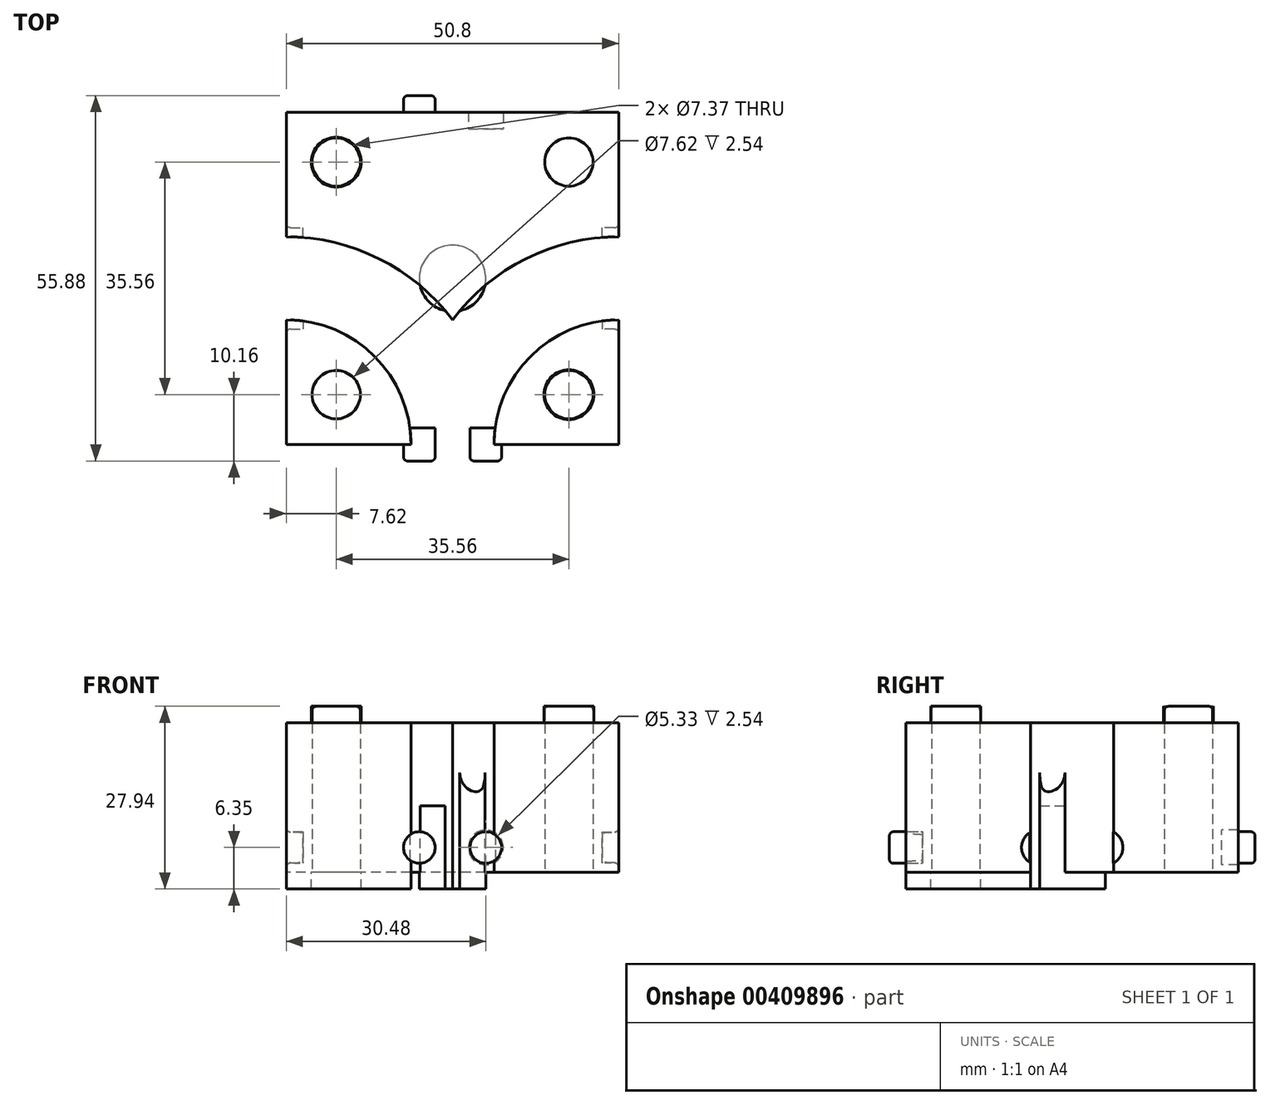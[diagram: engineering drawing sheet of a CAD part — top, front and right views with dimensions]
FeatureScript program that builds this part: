
annotation { "Feature Type Name" : "Feature", "Feature Type Description" : "" }
export const myFeature = defineFeature(function(context is Context, id is Id, definition is map)
    precondition{}
    {
        {
            var Q0;
            Q0=qCreatedBy(makeId("Top.planeOp"),FACE);
            var sketch = newSketch(context, id + "F0", { "sketchPlane" : qUnion([Q0])});
            skLineSegment(sketch, "E0.bottom", {"start": v(25.4, 25.4) * mm, "end": v(-25.4, 25.4) * mm});
            skLineSegment(sketch, "E0.top", {"start": v(25.4, -25.4) * mm, "end": v(-25.4, -25.4) * mm});
            skLineSegment(sketch, "E0.left", {"start": v(25.4, 25.4) * mm, "end": v(25.4, -25.4) * mm});
            skLineSegment(sketch, "E0.right", {"start": v(-25.4, 25.4) * mm, "end": v(-25.4, -25.4) * mm});
            skPoint(sketch, "E0.middle", {"position": v(0, 0) * mm});
            skPoint(sketch, "E1", {"position": v(17.78, 17.78) * mm});
            skPoint(sketch, "E2", {"position": v(17.78, 25.4) * mm});
            skLineSegment(sketch, "E3", {"start": v(17.78, 17.78) * mm, "end": v(17.78, 25.4) * mm, "construction": true});
            skCircle(sketch, "E4", {"center": v(17.78, 17.78) * mm, "radius": 3.81 * mm, "construction": true});
            skCircle(sketch, "E5.MirrorC", {"center": v(-17.78, 17.78) * mm, "radius": 3.81 * mm});
            skCircle(sketch, "E6.MirrorC", {"center": v(17.78, -17.78) * mm, "radius": 3.81 * mm});
            skCircle(sketch, "E7.MirrorC", {"center": v(-17.78, -17.78) * mm, "radius": 3.81 * mm});
            skPoint(sketch, "E8", {"position": v(25.4, 0) * mm});
            skPoint(sketch, "E9", {"position": v(-25.4, 0) * mm});
            skCircle(sketch, "E10", {"center": v(17.78, 17.78) * mm, "radius": 3.68 * mm});
            skCircle(sketch, "E11.MirrorC", {"center": v(-17.78, 17.78) * mm, "radius": 3.68 * mm});
            skCircle(sketch, "E12.MirrorC", {"center": v(-17.78, -17.78) * mm, "radius": 3.68 * mm});
            skCircle(sketch, "E13.MirrorC", {"center": v(17.78, -17.78) * mm, "radius": 3.68 * mm});
            skLineSegment(sketch, "E14", {"start": v(-25.4, 0) * mm, "end": v(25.4, 0) * mm, "construction": true});
            skLineSegment(sketch, "E15", {"start": v(0, 25.4) * mm, "end": v(0, -25.4) * mm, "construction": true});
            skCircle(sketch, "E16", {"center": v(0, 0) * mm, "radius": 2.54 * mm, "construction": true});
            skPoint(sketch, "E17", {"position": v(0, 2.54) * mm});
            skPoint(sketch, "E18", {"position": v(0, 5.08) * mm});
            skCircle(sketch, "E19", {"center": v(0, 0) * mm, "radius": 2.41 * mm});
            skCircle(sketch, "E20", {"center": v(0, 0) * mm, "radius": 2.67 * mm});
            skPoint(sketch, "E21", {"position": v(2.41, 0) * mm});
            skPoint(sketch, "E22", {"position": v(2.67, 0) * mm});
            skLineSegment(sketch, "E23", {"start": v(2.41, 0) * mm, "end": v(2.67, 0) * mm, "construction": true});
            skCircle(sketch, "E24", {"center": v(17.78, 17.78) * mm, "radius": 3.94 * mm});
            skLineSegment(sketch, "E25", {"start": v(17.78, 21.46) * mm, "end": v(17.78, 21.72) * mm, "construction": true});
            skPoint(sketch, "E25.endSnap0", {"position": v(17.78, 21.59) * mm});
            skLineSegment(sketch, "E26", {"start": v(25.4, 6.35) * mm, "end": v(25.4, -6.35) * mm});
            skPoint(sketch, "E27", {"position": v(6.35, -25.4) * mm});
            skPoint(sketch, "E28", {"position": v(-6.35, -25.4) * mm});
            skArc(sketch, "E29", {"start": v(6.35, -25.4) * mm, "mid": v(11.93, -11.93) * mm, "end": v(25.4, -6.35) * mm});
            skArc(sketch, "E30", {"start": v(-6.35, -25.4) * mm, "mid": v(-11.93, -11.93) * mm, "end": v(-25.4, -6.35) * mm});
            skPoint(sketch, "E31", {"position": v(-25.4, 6.35) * mm});
            skArc(sketch, "E32", {"start": v(25.4, 6.35) * mm, "mid": v(11.2, 3) * mm, "end": v(0, -6.35) * mm});
            skArc(sketch, "E33", {"start": v(0, -6.35) * mm, "mid": v(-11.2, 3) * mm, "end": v(-25.4, 6.35) * mm});
            skCircle(sketch, "E34", {"center": v(0, 0) * mm, "radius": 5.08 * mm});
            skPoint(sketch, "E35", {"position": v(2.54, 0) * mm});
            skLineSegment(sketch, "E36", {"start": v(17.78, 17.78) * mm, "end": v(25.4, 17.78) * mm});
            skSolve(sketch);
        }
        {
            var Q0;
            Q0=makeQuery(id+"F0.imprint","IMPRINT",FACE,{"disambiguationData":[TD([[makeQuery(id+"F0.imprint","IMPRINT",EDGE,{"derivedFrom":sQuery(id+"F0.wireOp",EDGE,"E5.MirrorC")}),1.0]])]});
            var Q1;
            {var subQ0=sQuery(id+"F0.wireOp",EDGE,"e8c6bd5a-b162-413f-9673-ee5317453a08.1.0");var subQ1=sQuery(id+"F0.wireOp",EDGE,"E0.right");var subQ2=makeQuery(id+"F0.imprint","INTERSECT",VERTEX,{"derivedFrom":[subQ1,subQ0]});Q1=makeQuery(id+"F0.imprint","IMPRINT",FACE,{"disambiguationData":[TD([[makeQuery(id+"F0.imprint","IMPRINT",EDGE,{"disambiguationData":[TD([[subQ2,-1.0]])],"derivedFrom":subQ1}),1.0]])]});}
            var Q2;
            Q2=makeQuery(id+"F0.imprint","IMPRINT",FACE,{"disambiguationData":[TD([[makeQuery(id+"F0.imprint","IMPRINT",EDGE,{"derivedFrom":sQuery(id+"F0.wireOp",EDGE,"E7.MirrorC")}),-1.0]])]});
            var Q3;
            Q3=makeQuery(id+"F0.imprint","IMPRINT",FACE,{"disambiguationData":[TD([[makeQuery(id+"F0.imprint","IMPRINT",EDGE,{"derivedFrom":sQuery(id+"F0.wireOp",EDGE,"E5.MirrorC")}),-1.0]])]});
            var Q4;
            Q4=makeQuery(id+"F0.imprint","IMPRINT",FACE,{"disambiguationData":[TD([[makeQuery(id+"F0.imprint","IMPRINT",EDGE,{"derivedFrom":sQuery(id+"F0.wireOp",EDGE,"E7.MirrorC")}),1.0]])]});
            var Q5;
            Q5=makeQuery(id+"F0.imprint","IMPRINT",FACE,{"disambiguationData":[TD([[makeQuery(id+"F0.imprint","IMPRINT",EDGE,{"derivedFrom":sQuery(id+"F0.wireOp",EDGE,"E6.MirrorC")}),-1.0]])]});
            var Q6;
            Q6=makeQuery(id+"F0.imprint","IMPRINT",FACE,{"disambiguationData":[TD([[makeQuery(id+"F0.imprint","IMPRINT",EDGE,{"derivedFrom":sQuery(id+"F0.wireOp",EDGE,"E10")}),-1.0]])]});
            var Q7;
            Q7=makeQuery(id+"F0.imprint","IMPRINT",FACE,{"disambiguationData":[TD([[makeQuery(id+"F0.imprint","IMPRINT",EDGE,{"derivedFrom":sQuery(id+"F0.wireOp",EDGE,"E19")}),1.0]])]});
            var Q8;
            Q8=makeQuery(id+"F0.imprint","IMPRINT",FACE,{"disambiguationData":[TD([[makeQuery(id+"F0.imprint","IMPRINT",EDGE,{"derivedFrom":sQuery(id+"F0.wireOp",EDGE,"E12.MirrorC")}),1.0]])]});
            var Q9;
            Q9=makeQuery(id+"F0.imprint","IMPRINT",FACE,{"disambiguationData":[TD([[makeQuery(id+"F0.imprint","IMPRINT",EDGE,{"derivedFrom":sQuery(id+"F0.wireOp",EDGE,"E7.MirrorC")}),-1.0]])]});
            var Q10;
            Q10=makeQuery(id+"F0.imprint","IMPRINT",FACE,{"disambiguationData":[TD([[makeQuery(id+"F0.imprint","IMPRINT",EDGE,{"derivedFrom":sQuery(id+"F0.wireOp",EDGE,"E13.MirrorC")}),-1.0]])]});
            var Q11;
            Q11=makeQuery(id+"F0.imprint","IMPRINT",FACE,{"disambiguationData":[TD([[makeQuery(id+"F0.imprint","IMPRINT",EDGE,{"derivedFrom":sQuery(id+"F0.wireOp",EDGE,"E6.MirrorC")}),1.0]])]});
            var Q12;
            Q12=makeQuery(id+"F0.imprint","IMPRINT",FACE,{"disambiguationData":[TD([[makeQuery(id+"F0.imprint","IMPRINT",EDGE,{"derivedFrom":sQuery(id+"F0.wireOp",EDGE,"E11.MirrorC")}),-1.0]])]});
            var Q13;
            Q13=makeQuery(id+"F0.imprint","IMPRINT",FACE,{"disambiguationData":[TD([[makeQuery(id+"F0.imprint","IMPRINT",EDGE,{"derivedFrom":sQuery(id+"F0.wireOp",EDGE,"E10")}),1.0]])]});
            var Q14;
            Q14=makeQuery(id+"F0.imprint","IMPRINT",FACE,{"disambiguationData":[TD([[makeQuery(id+"F0.imprint","IMPRINT",EDGE,{"derivedFrom":sQuery(id+"F0.wireOp",EDGE,"E19")}),-1.0]])]});
            var Q15;
            Q15=makeQuery(id+"F0.imprint","IMPRINT",FACE,{"disambiguationData":[TD([[makeQuery(id+"F0.imprint","IMPRINT",EDGE,{"derivedFrom":sQuery(id+"F0.wireOp",EDGE,"E20")}),-1.0]])]});
            var Q16;
            {var subQ0=sQuery(id+"F0.wireOp",EDGE,"E33");var subQ1=sQuery(id+"F0.wireOp",EDGE,"E32");var subQ2=makeQuery(id+"F0.imprint","INTERSECT",VERTEX,{"derivedFrom":[subQ1,subQ0]});Q16=makeQuery(id+"F0.imprint","IMPRINT",FACE,{"disambiguationData":[TD([[makeQuery(id+"F0.imprint","IMPRINT",EDGE,{"disambiguationData":[TD([[subQ2,1.0]])],"derivedFrom":subQ1}),-1.0]])]});}
            extrude(context, id + "F1", {"entities" : qUnion([Q0, Q1, Q2, Q3, Q4, Q5, Q6, Q7, Q8, Q9, Q10, Q11, Q12, Q13, Q14, Q15, Q16]), "depth" : 12.7 * mm});
        }
        {
            var Q0;
            Q0=makeQuery(id+"F0.imprint","IMPRINT",FACE,{"disambiguationData":[TD([[makeQuery(id+"F0.imprint","IMPRINT",EDGE,{"derivedFrom":sQuery(id+"F0.wireOp",EDGE,"E12.MirrorC")}),1.0]])]});
            var Q1;
            Q1=makeQuery(id+"F0.imprint","IMPRINT",FACE,{"disambiguationData":[TD([[makeQuery(id+"F0.imprint","IMPRINT",EDGE,{"derivedFrom":sQuery(id+"F0.wireOp",EDGE,"E11.MirrorC")}),-1.0]])]});
            var Q2;
            Q2=makeQuery(id+"F0.imprint","IMPRINT",FACE,{"disambiguationData":[TD([[makeQuery(id+"F0.imprint","IMPRINT",EDGE,{"derivedFrom":sQuery(id+"F0.wireOp",EDGE,"E10")}),1.0]])]});
            var Q3;
            Q3=makeQuery(id+"F0.imprint","IMPRINT",FACE,{"disambiguationData":[TD([[makeQuery(id+"F0.imprint","IMPRINT",EDGE,{"derivedFrom":sQuery(id+"F0.wireOp",EDGE,"E13.MirrorC")}),-1.0]])]});
            extrude(context, id + "F2", {"entities" : qUnion([Q0, Q1, Q2, Q3]), "operationType" : NewBodyOperationType.ADD, "depth" : 15.24 * mm});
        }
        {
            var Q0;
            Q0=makeQuery(id+"F0.imprint","IMPRINT",FACE,{"disambiguationData":[TD([[makeQuery(id+"F0.imprint","IMPRINT",EDGE,{"derivedFrom":sQuery(id+"F0.wireOp",EDGE,"E7.MirrorC")}),-1.0]])]});
            var Q1;
            Q1=makeQuery(id+"F0.imprint","IMPRINT",FACE,{"disambiguationData":[TD([[makeQuery(id+"F0.imprint","IMPRINT",EDGE,{"derivedFrom":sQuery(id+"F0.wireOp",EDGE,"E19")}),-1.0]])]});
            var Q2;
            Q2=makeQuery(id+"F0.imprint","IMPRINT",FACE,{"disambiguationData":[TD([[makeQuery(id+"F0.imprint","IMPRINT",EDGE,{"derivedFrom":sQuery(id+"F0.wireOp",EDGE,"E19")}),1.0]])]});
            var Q3;
            {var subQ1=sQuery(id+"F0.wireOp",EDGE,"E0.bottom");Q3=makeQuery(id+"F0.imprint","IMPRINT",FACE,{"disambiguationData":[TD([[makeQuery(id+"F0.imprint","IMPRINT",EDGE,{"derivedFrom":subQ1}),1.0]])]});}
            var Q4;
            {var subQ4=sQuery(id+"F0.wireOp",EDGE,"E26");Q4=makeQuery(id+"F0.imprint","IMPRINT",FACE,{"disambiguationData":[TD([[makeQuery(id+"F0.imprint","IMPRINT",EDGE,{"derivedFrom":subQ4}),-1.0]])]});}
            var Q5;
            Q5=makeQuery(id+"F0.imprint","IMPRINT",FACE,{"disambiguationData":[TD([[makeQuery(id+"F0.imprint","IMPRINT",EDGE,{"derivedFrom":sQuery(id+"F0.wireOp",EDGE,"E13.MirrorC")}),-1.0]])]});
            var Q6;
            Q6=makeQuery(id+"F0.imprint","IMPRINT",FACE,{"disambiguationData":[TD([[makeQuery(id+"F0.imprint","IMPRINT",EDGE,{"derivedFrom":sQuery(id+"F0.wireOp",EDGE,"E6.MirrorC")}),-1.0]])]});
            var Q7;
            Q7=makeQuery(id+"F0.imprint","IMPRINT",FACE,{"disambiguationData":[TD([[makeQuery(id+"F0.imprint","IMPRINT",EDGE,{"derivedFrom":sQuery(id+"F0.wireOp",EDGE,"E6.MirrorC")}),1.0]])]});
            var Q8;
            Q8=makeQuery(id+"F0.imprint","IMPRINT",FACE,{"disambiguationData":[TD([[makeQuery(id+"F0.imprint","IMPRINT",EDGE,{"derivedFrom":sQuery(id+"F0.wireOp",EDGE,"E12.MirrorC")}),1.0]])]});
            var Q9;
            Q9=makeQuery(id+"F0.imprint","IMPRINT",FACE,{"disambiguationData":[TD([[makeQuery(id+"F0.imprint","IMPRINT",EDGE,{"derivedFrom":sQuery(id+"F0.wireOp",EDGE,"E7.MirrorC")}),1.0]])]});
            var Q10;
            Q10=makeQuery(id+"F0.imprint","IMPRINT",FACE,{"disambiguationData":[TD([[makeQuery(id+"F0.imprint","IMPRINT",EDGE,{"derivedFrom":sQuery(id+"F0.wireOp",EDGE,"E5.MirrorC")}),-1.0]])]});
            var Q11;
            Q11=makeQuery(id+"F0.imprint","IMPRINT",FACE,{"disambiguationData":[TD([[makeQuery(id+"F0.imprint","IMPRINT",EDGE,{"derivedFrom":sQuery(id+"F0.wireOp",EDGE,"E11.MirrorC")}),-1.0]])]});
            var Q12;
            Q12=makeQuery(id+"F0.imprint","IMPRINT",FACE,{"disambiguationData":[TD([[makeQuery(id+"F0.imprint","IMPRINT",EDGE,{"derivedFrom":sQuery(id+"F0.wireOp",EDGE,"E10")}),-1.0]])]});
            var Q13;
            Q13=makeQuery(id+"F0.imprint","IMPRINT",FACE,{"disambiguationData":[TD([[makeQuery(id+"F0.imprint","IMPRINT",EDGE,{"derivedFrom":sQuery(id+"F0.wireOp",EDGE,"E10")}),1.0]])]});
            var Q14;
            Q14=makeQuery(id+"F0.imprint","IMPRINT",FACE,{"disambiguationData":[TD([[makeQuery(id+"F0.imprint","IMPRINT",EDGE,{"derivedFrom":sQuery(id+"F0.wireOp",EDGE,"E20")}),-1.0]])]});
            var Q15;
            {var subQ0=sQuery(id+"F0.wireOp",EDGE,"E34");var subQ1=sQuery(id+"F0.wireOp",EDGE,"E33");var subQ2=makeQuery(id+"F0.imprint","INTERSECT",VERTEX,{"disambiguationData":[OD(0.0)],"derivedFrom":[subQ1,subQ0]});Q15=makeQuery(id+"F0.imprint","IMPRINT",FACE,{"disambiguationData":[TD([[makeQuery(id+"F0.imprint","IMPRINT",EDGE,{"disambiguationData":[TD([[subQ2,-1.0]])],"derivedFrom":subQ1}),1.0]])]});}
            var Q16;
            {var subQ0=sQuery(id+"F0.wireOp",EDGE,"E34");var subQ1=sQuery(id+"F0.wireOp",EDGE,"E32");var subQ2=makeQuery(id+"F0.imprint","INTERSECT",VERTEX,{"disambiguationData":[OD(0.0)],"derivedFrom":[subQ1,subQ0]});Q16=makeQuery(id+"F0.imprint","IMPRINT",FACE,{"disambiguationData":[TD([[makeQuery(id+"F0.imprint","IMPRINT",EDGE,{"disambiguationData":[TD([[subQ2,-1.0]])],"derivedFrom":subQ1}),1.0]])]});}
            var Q17;
            {var subQ0=sQuery(id+"F0.wireOp",EDGE,"E33");var subQ1=sQuery(id+"F0.wireOp",EDGE,"E32");var subQ2=makeQuery(id+"F0.imprint","INTERSECT",VERTEX,{"derivedFrom":[subQ1,subQ0]});Q17=makeQuery(id+"F0.imprint","IMPRINT",FACE,{"disambiguationData":[TD([[makeQuery(id+"F0.imprint","IMPRINT",EDGE,{"disambiguationData":[TD([[subQ2,1.0]])],"derivedFrom":subQ1}),-1.0]])]});}
            extrude(context, id + "F3", {"entities" : qUnion([Q0, Q1, Q2, Q3, Q4, Q5, Q6, Q7, Q8, Q9, Q10, Q11, Q12, Q13, Q14, Q15, Q16, Q17]), "operationType" : NewBodyOperationType.ADD, "oppositeDirection" : true, "depth" : 12.7 * mm});
        }
        {
            var Q0;
            Q0=makeQuery(id+"F0.imprint","IMPRINT",FACE,{"disambiguationData":[TD([[makeQuery(id+"F0.imprint","IMPRINT",EDGE,{"derivedFrom":sQuery(id+"F0.wireOp",EDGE,"E13.MirrorC")}),-1.0]])]});
            var Q1;
            Q1=makeQuery(id+"F0.imprint","IMPRINT",FACE,{"disambiguationData":[TD([[makeQuery(id+"F0.imprint","IMPRINT",EDGE,{"derivedFrom":sQuery(id+"F0.wireOp",EDGE,"E7.MirrorC")}),1.0]])]});
            var Q2;
            Q2=makeQuery(id+"F0.imprint","IMPRINT",FACE,{"disambiguationData":[TD([[makeQuery(id+"F0.imprint","IMPRINT",EDGE,{"derivedFrom":sQuery(id+"F0.wireOp",EDGE,"E12.MirrorC")}),1.0]])]});
            var Q3;
            Q3=makeQuery(id+"F0.imprint","IMPRINT",FACE,{"disambiguationData":[TD([[makeQuery(id+"F0.imprint","IMPRINT",EDGE,{"derivedFrom":sQuery(id+"F0.wireOp",EDGE,"E6.MirrorC")}),-1.0]])]});
            var Q4;
            Q4=makeQuery(id+"F0.imprint","IMPRINT",FACE,{"disambiguationData":[TD([[makeQuery(id+"F0.imprint","IMPRINT",EDGE,{"derivedFrom":sQuery(id+"F0.wireOp",EDGE,"E10")}),-1.0]])]});
            var Q5;
            Q5=makeQuery(id+"F0.imprint","IMPRINT",FACE,{"disambiguationData":[TD([[makeQuery(id+"F0.imprint","IMPRINT",EDGE,{"derivedFrom":sQuery(id+"F0.wireOp",EDGE,"E10")}),1.0]])]});
            var Q6;
            Q6=makeQuery(id+"F0.imprint","IMPRINT",FACE,{"disambiguationData":[TD([[makeQuery(id+"F0.imprint","IMPRINT",EDGE,{"derivedFrom":sQuery(id+"F0.wireOp",EDGE,"E5.MirrorC")}),-1.0]])]});
            var Q7;
            Q7=makeQuery(id+"F0.imprint","IMPRINT",FACE,{"disambiguationData":[TD([[makeQuery(id+"F0.imprint","IMPRINT",EDGE,{"derivedFrom":sQuery(id+"F0.wireOp",EDGE,"E11.MirrorC")}),-1.0]])]});
            extrude(context, id + "F4", {"entities" : qUnion([Q0, Q1, Q2, Q3, Q4, Q5, Q6, Q7]), "operationType" : NewBodyOperationType.REMOVE, "oppositeDirection" : true, "depth" : 12.7 * mm, "hasSecondDirection" : true, "secondDirectionOppositeDirection" : true, "secondDirectionDepth" : 10.16 * mm});
        }
        {
            var Q0;
            Q0=qCreatedBy(makeId("Right.planeOp"),FACE);
            var sketch = newSketch(context, id + "F5", { "sketchPlane" : qUnion([Q0])});
            skLineSegment(sketch, "E37", {"start": v(-25.4, 12.7) * mm, "end": v(-25.4, -12.7) * mm, "construction": true});
            skPoint(sketch, "E38", {"position": v(-25.4, 0) * mm});
            skPoint(sketch, "E39", {"position": v(-25.4, -6.35) * mm});
            skLineSegment(sketch, "E40", {"start": v(-2.41, 0) * mm, "end": v(-2.67, 0) * mm, "construction": true});
            skLineSegment(sketch, "E41", {"start": v(2.67, 0) * mm, "end": v(2.41, 0) * mm, "construction": true});
            skPoint(sketch, "E42", {"position": v(-5.08, -6.35) * mm});
            skPoint(sketch, "E43", {"position": v(-2.67, -6.35) * mm});
            skPoint(sketch, "E44", {"position": v(-2.41, -6.35) * mm});
            skPoint(sketch, "E45", {"position": v(2.41, -6.35) * mm});
            skPoint(sketch, "E46", {"position": v(2.67, -6.35) * mm});
            skPoint(sketch, "E47", {"position": v(5.08, -6.35) * mm});
            skCircle(sketch, "E48", {"center": v(-5.08, -6.35) * mm, "radius": 2.41 * mm});
            skCircle(sketch, "E49", {"center": v(-5.08, -6.35) * mm, "radius": 2.67 * mm});
            skCircle(sketch, "E50", {"center": v(5.08, -6.35) * mm, "radius": 2.41 * mm});
            skCircle(sketch, "E51", {"center": v(5.08, -6.35) * mm, "radius": 2.67 * mm});
            skLineSegment(sketch, "E52", {"start": v(25.4, 12.7) * mm, "end": v(25.4, -12.7) * mm});
            skPoint(sketch, "E53", {"position": v(25.4, 0) * mm});
            skPoint(sketch, "E54", {"position": v(25.4, -6.35) * mm});
            skLineSegment(sketch, "E55", {"start": v(-2.67, 0) * mm, "end": v(-5.08, 0) * mm});
            skLineSegment(sketch, "E56", {"start": v(5.08, 0) * mm, "end": v(2.67, 0) * mm});
            skSolve(sketch);
        }
        {
            var Q0;
            Q0=qCreatedBy(makeId("Front.planeOp"),FACE);
            var sketch = newSketch(context, id + "F6", { "sketchPlane" : qUnion([Q0])});
            skLineSegment(sketch, "E57", {"start": v(-25.4, -12.7) * mm, "end": v(-25.4, 12.7) * mm, "construction": true});
            skLineSegment(sketch, "E58", {"start": v(25.4, -12.7) * mm, "end": v(25.4, 0) * mm, "construction": true});
            skPoint(sketch, "E59", {"position": v(25.4, -6.35) * mm});
            skPoint(sketch, "E60", {"position": v(-25.4, 0) * mm});
            skPoint(sketch, "E61", {"position": v(-25.4, -6.35) * mm});
            skLineSegment(sketch, "E62", {"start": v(-2.41, 0) * mm, "end": v(-2.67, 0) * mm, "construction": true});
            skLineSegment(sketch, "E63", {"start": v(2.67, 0) * mm, "end": v(2.41, 0) * mm, "construction": true});
            skPoint(sketch, "E64", {"position": v(5.08, -6.35) * mm});
            skPoint(sketch, "E65", {"position": v(2.67, -6.35) * mm});
            skPoint(sketch, "E66", {"position": v(2.41, -6.35) * mm});
            skPoint(sketch, "E67", {"position": v(-2.41, -6.35) * mm});
            skPoint(sketch, "E68", {"position": v(-2.67, -6.35) * mm});
            skPoint(sketch, "E69", {"position": v(-5.08, -6.35) * mm});
            skCircle(sketch, "E70", {"center": v(5.08, -6.35) * mm, "radius": 2.41 * mm});
            skCircle(sketch, "E71", {"center": v(5.08, -6.35) * mm, "radius": 2.67 * mm});
            skCircle(sketch, "E72", {"center": v(-5.08, -6.35) * mm, "radius": 2.67 * mm});
            skCircle(sketch, "E73", {"center": v(-5.08, -6.35) * mm, "radius": 2.41 * mm});
            skLineSegment(sketch, "E74", {"start": v(-2.67, 0) * mm, "end": v(-5.08, 0) * mm});
            skLineSegment(sketch, "E75", {"start": v(5.08, 0) * mm, "end": v(2.67, 0) * mm});
            skSolve(sketch);
        }
        {
            var Q0;
            Q0=makeQuery(id+"F6.imprint","IMPRINT",FACE,{"disambiguationData":[TD([[makeQuery(id+"F6.imprint","IMPRINT",EDGE,{"derivedFrom":sQuery(id+"F6.wireOp",EDGE,"E73")}),1.0]])]});
            extrude(context, id + "F7", {"entities" : qUnion([Q0]), "operationType" : NewBodyOperationType.ADD, "oppositeDirection" : true, "depth" : 27.94 * mm, "hasSecondDirection" : true, "secondDirectionOppositeDirection" : true, "secondDirectionDepth" : 22.86 * mm});
        }
        {
            var Q0;
            Q0=makeQuery(id+"F6.imprint","IMPRINT",FACE,{"disambiguationData":[TD([[makeQuery(id+"F6.imprint","IMPRINT",EDGE,{"derivedFrom":sQuery(id+"F6.wireOp",EDGE,"E73")}),1.0]])]});
            var Q1;
            Q1=makeQuery(id+"F6.imprint","IMPRINT",FACE,{"disambiguationData":[TD([[makeQuery(id+"F6.imprint","IMPRINT",EDGE,{"derivedFrom":sQuery(id+"F6.wireOp",EDGE,"E70")}),1.0]])]});
            extrude(context, id + "F8", {"entities" : qUnion([Q0, Q1]), "operationType" : NewBodyOperationType.ADD, "depth" : 27.94 * mm, "hasSecondDirection" : true, "secondDirectionOppositeDirection" : false, "secondDirectionDepth" : 22.86 * mm});
        }
        {
            var Q0;
            Q0=makeQuery(id+"F5.imprint","IMPRINT",FACE,{"disambiguationData":[TD([[makeQuery(id+"F5.imprint","IMPRINT",EDGE,{"derivedFrom":sQuery(id+"F5.wireOp",EDGE,"E48")}),1.0]])]});
            var Q1;
            Q1=makeQuery(id+"F5.imprint","IMPRINT",FACE,{"disambiguationData":[TD([[makeQuery(id+"F5.imprint","IMPRINT",EDGE,{"derivedFrom":sQuery(id+"F5.wireOp",EDGE,"E50")}),1.0]])]});
            var Q2;
            Q2=makeQuery(id+"F5.imprint","IMPRINT",FACE,{"disambiguationData":[TD([[makeQuery(id+"F5.imprint","IMPRINT",EDGE,{"derivedFrom":sQuery(id+"F5.wireOp",EDGE,"E48")}),-1.0]])]});
            var Q3;
            Q3=makeQuery(id+"F5.imprint","IMPRINT",FACE,{"disambiguationData":[TD([[makeQuery(id+"F5.imprint","IMPRINT",EDGE,{"derivedFrom":sQuery(id+"F5.wireOp",EDGE,"E50")}),-1.0]])]});
            extrude(context, id + "F9", {"entities" : qUnion([Q0, Q1, Q2, Q3]), "operationType" : NewBodyOperationType.REMOVE, "depth" : 27.94 * mm, "hasSecondDirection" : true, "secondDirectionOppositeDirection" : false, "secondDirectionDepth" : 22.86 * mm});
        }
        {
            var Q0;
            Q0=makeQuery(id+"F5.imprint","IMPRINT",FACE,{"disambiguationData":[TD([[makeQuery(id+"F5.imprint","IMPRINT",EDGE,{"derivedFrom":sQuery(id+"F5.wireOp",EDGE,"E48")}),-1.0]])]});
            var Q1;
            Q1=makeQuery(id+"F5.imprint","IMPRINT",FACE,{"disambiguationData":[TD([[makeQuery(id+"F5.imprint","IMPRINT",EDGE,{"derivedFrom":sQuery(id+"F5.wireOp",EDGE,"E48")}),1.0]])]});
            var Q2;
            Q2=makeQuery(id+"F5.imprint","IMPRINT",FACE,{"disambiguationData":[TD([[makeQuery(id+"F5.imprint","IMPRINT",EDGE,{"derivedFrom":sQuery(id+"F5.wireOp",EDGE,"E50")}),1.0]])]});
            var Q3;
            Q3=makeQuery(id+"F5.imprint","IMPRINT",FACE,{"disambiguationData":[TD([[makeQuery(id+"F5.imprint","IMPRINT",EDGE,{"derivedFrom":sQuery(id+"F5.wireOp",EDGE,"E50")}),-1.0]])]});
            extrude(context, id + "F10", {"entities" : qUnion([Q0, Q1, Q2, Q3]), "operationType" : NewBodyOperationType.REMOVE, "oppositeDirection" : true, "depth" : 27.94 * mm, "hasSecondDirection" : true, "secondDirectionOppositeDirection" : true, "secondDirectionDepth" : 22.86 * mm});
        }
        {
            var Q0;
            Q0=makeQuery(id+"F6.imprint","IMPRINT",FACE,{"disambiguationData":[TD([[makeQuery(id+"F6.imprint","IMPRINT",EDGE,{"derivedFrom":sQuery(id+"F6.wireOp",EDGE,"E70")}),1.0]])]});
            var Q1;
            Q1=makeQuery(id+"F6.imprint","IMPRINT",FACE,{"disambiguationData":[TD([[makeQuery(id+"F6.imprint","IMPRINT",EDGE,{"derivedFrom":sQuery(id+"F6.wireOp",EDGE,"E70")}),-1.0]])]});
            extrude(context, id + "F11", {"entities" : qUnion([Q0, Q1]), "operationType" : NewBodyOperationType.REMOVE, "oppositeDirection" : true, "depth" : 27.94 * mm, "hasSecondDirection" : true, "secondDirectionOppositeDirection" : true, "secondDirectionDepth" : 22.86 * mm});
        }
        {
            var Q0;
            Q0=makeQuery(id+"F1.opExtrude","CAP_EDGE",EDGE,{"disambiguationData":[OSD([sQuery(id+"F0.wireOp",EDGE,"E29")])],"isStart":true});
            var Q1;
            Q1=makeQuery(id+"F1.opExtrude","CAP_EDGE",EDGE,{"disambiguationData":[OSD([sQuery(id+"F0.wireOp",EDGE,"E30")])],"isStart":true});
            var Q2;
            Q2=makeQuery(id+"F1.opExtrude","CAP_EDGE",EDGE,{"disambiguationData":[OSD([sQuery(id+"F0.wireOp",EDGE,"E33")])],"isStart":true});
            var Q3;
            Q3=makeQuery(id+"F1.opExtrude","CAP_EDGE",EDGE,{"disambiguationData":[OSD([sQuery(id+"F0.wireOp",EDGE,"E32")])],"isStart":true});
            fillet(context, id + "F12", {"entities" : qUnion([Q0, Q1, Q2, Q3]), "radius" : 5.08 * mm, "tangentPropagation" : true, "allowEdgeOverflow" : false});
        }
        {
            var Q0;
            Q0=makeQuery(id+"F2.opExtrude","CAP_EDGE",EDGE,{"disambiguationData":[OSD([sQuery(id+"F0.wireOp",EDGE,"E13.MirrorC")])],"isStart":false});
            var Q1;
            Q1=makeQuery(id+"F2.opExtrude","CAP_EDGE",EDGE,{"disambiguationData":[OSD([sQuery(id+"F0.wireOp",EDGE,"E12.MirrorC")])],"isStart":false});
            var Q2;
            Q2=makeQuery(id+"F2.opExtrude","CAP_EDGE",EDGE,{"disambiguationData":[OSD([sQuery(id+"F0.wireOp",EDGE,"E11.MirrorC")])],"isStart":false});
            var Q3;
            Q3=makeQuery(id+"F2.opExtrude","CAP_EDGE",EDGE,{"disambiguationData":[OSD([sQuery(id+"F0.wireOp",EDGE,"E10")])],"isStart":false});
            var Q4;
            Q4=makeQuery(id+"F7.opExtrude","CAP_EDGE",EDGE,{"disambiguationData":[OSD([sQuery(id+"F6.wireOp",EDGE,"E73")])],"isStart":false});
            var Q5;
            {var subQ0=sQuery(id+"F0.wireOp",EDGE,"E0.right");Q5=makeQuery(id+"F10.boolean.opBoolean","INTERSECT",EDGE,{"derivedFrom":[makeQuery(id+"FVeaqIvGeaTVGBi_11.opBoolean","MERGE",FACE,{"derivedFrom":[makeQuery(id+"F1.opExtrude","SWEPT_FACE",FACE,{"disambiguationData":[OSD([subQ0])]}),makeQuery(id+"F3.opExtrude","SWEPT_FACE",FACE,{"disambiguationData":[OSD([subQ0])]})]}),makeQuery(id+"F10.opExtrude","SWEPT_FACE",FACE,{"disambiguationData":[OSD([sQuery(id+"F5.wireOp",EDGE,"E49")])]})]});}
            var Q6;
            {var subQ0=sQuery(id+"F0.wireOp",EDGE,"E0.top");Q6=makeQuery(id+"F11.boolean.opBoolean","INTERSECT",EDGE,{"derivedFrom":[makeQuery(id+"FVeaqIvGeaTVGBi_11.opBoolean","MERGE",FACE,{"derivedFrom":[makeQuery(id+"F1.opExtrude","SWEPT_FACE",FACE,{"disambiguationData":[OSD([subQ0])]}),makeQuery(id+"F3.opExtrude","SWEPT_FACE",FACE,{"disambiguationData":[OSD([subQ0])]})]}),makeQuery(id+"F11.opExtrude","SWEPT_FACE",FACE,{"disambiguationData":[OSD([sQuery(id+"F6.wireOp",EDGE,"E71")])]})]});}
            var Q7;
            {var subQ0=sQuery(id+"F0.wireOp",EDGE,"E0.right");Q7=makeQuery(id+"F10.boolean.opBoolean","INTERSECT",EDGE,{"derivedFrom":[makeQuery(id+"FVeaqIvGeaTVGBi_11.opBoolean","MERGE",FACE,{"derivedFrom":[makeQuery(id+"F1.opExtrude","SWEPT_FACE",FACE,{"disambiguationData":[OSD([subQ0]),TDD([makeQuery(id+"F0.imprint","IMPRINT",EDGE,{"disambiguationData":[TD([[makeQuery(id+"F0.imprint","INTERSECT",VERTEX,{"derivedFrom":[sQuery(id+"F0.wireOp",EDGE,"E0.bottom"),subQ0]}),-1.0]])],"derivedFrom":subQ0})])]}),makeQuery(id+"F1.opExtrude","SWEPT_FACE",FACE,{"disambiguationData":[OSD([subQ0]),TDD([makeQuery(id+"F0.imprint","IMPRINT",EDGE,{"disambiguationData":[TD([[makeQuery(id+"F0.imprint","INTERSECT",VERTEX,{"derivedFrom":[sQuery(id+"F0.wireOp",EDGE,"E0.top"),subQ0]}),1.0]])],"derivedFrom":subQ0})])]}),makeQuery(id+"F3.opExtrude","SWEPT_FACE",FACE,{"disambiguationData":[OSD([subQ0])]})]}),makeQuery(id+"F10.opExtrude","SWEPT_FACE",FACE,{"disambiguationData":[OSD([sQuery(id+"F5.wireOp",EDGE,"E51")])]})]});}
            var Q8;
            Q8=makeQuery(id+"F8.opExtrude","CAP_EDGE",EDGE,{"disambiguationData":[OSD([sQuery(id+"F6.wireOp",EDGE,"E70")])],"isStart":false});
            var Q9;
            Q9=makeQuery(id+"F8.opExtrude","CAP_EDGE",EDGE,{"disambiguationData":[OSD([sQuery(id+"F6.wireOp",EDGE,"E73")])],"isStart":false});
            var Q10;
            {var subQ0=sQuery(id+"F0.wireOp",EDGE,"E26");var subQ1=sQuery(id+"F0.wireOp",EDGE,"E0.left");Q10=makeQuery(id+"F9.boolean.opBoolean","INTERSECT",EDGE,{"derivedFrom":[makeQuery(id+"FVeaqIvGeaTVGBi_11.opBoolean","MERGE",FACE,{"derivedFrom":[makeQuery(id+"F1.opExtrude","SWEPT_FACE",FACE,{"disambiguationData":[OSD([subQ1]),TDD([makeQuery(id+"F0.imprint","IMPRINT",EDGE,{"disambiguationData":[TD([[makeQuery(id+"F0.imprint","INTERSECT",VERTEX,{"derivedFrom":[subQ1,sQuery(id+"F0.wireOp",EDGE,"lMXQf7WU-VQvn-eUw7-3v8j-XpuHpQXpMMjl")]}),-1.0]])],"derivedFrom":subQ1})])]}),makeQuery(id+"F1.opExtrude","SWEPT_FACE",FACE,{"disambiguationData":[OSD([subQ1]),TDD([makeQuery(id+"F0.imprint","IMPRINT",EDGE,{"disambiguationData":[TD([[makeQuery(id+"F0.imprint","INTERSECT",VERTEX,{"derivedFrom":[sQuery(id+"F0.wireOp",EDGE,"E0.top"),subQ1]}),1.0]])],"derivedFrom":subQ1})])]}),makeQuery(id+"F3.opExtrude","SWEPT_FACE",FACE,{"disambiguationData":[OSD([subQ1,subQ0])]})]}),makeQuery(id+"F9.opExtrude","SWEPT_FACE",FACE,{"disambiguationData":[OSD([sQuery(id+"F5.wireOp",EDGE,"E49")])]})]});}
            var Q11;
            {var subQ0=sQuery(id+"F0.wireOp",EDGE,"E26");var subQ1=sQuery(id+"F0.wireOp",EDGE,"E0.left");Q11=makeQuery(id+"F9.boolean.opBoolean","INTERSECT",EDGE,{"derivedFrom":[makeQuery(id+"FVeaqIvGeaTVGBi_11.opBoolean","MERGE",FACE,{"derivedFrom":[makeQuery(id+"F1.opExtrude","SWEPT_FACE",FACE,{"disambiguationData":[OSD([subQ1]),TDD([makeQuery(id+"F0.imprint","IMPRINT",EDGE,{"disambiguationData":[TD([[makeQuery(id+"F0.imprint","INTERSECT",VERTEX,{"derivedFrom":[subQ1,sQuery(id+"F0.wireOp",EDGE,"lMXQf7WU-VQvn-eUw7-3v8j-XpuHpQXpMMjl")]}),-1.0]])],"derivedFrom":subQ1})])]}),makeQuery(id+"F1.opExtrude","SWEPT_FACE",FACE,{"disambiguationData":[OSD([subQ1]),TDD([makeQuery(id+"F0.imprint","IMPRINT",EDGE,{"disambiguationData":[TD([[makeQuery(id+"F0.imprint","INTERSECT",VERTEX,{"derivedFrom":[sQuery(id+"F0.wireOp",EDGE,"E0.top"),subQ1]}),1.0]])],"derivedFrom":subQ1})])]}),makeQuery(id+"F3.opExtrude","SWEPT_FACE",FACE,{"disambiguationData":[OSD([subQ1,subQ0])]})]}),makeQuery(id+"F9.opExtrude","SWEPT_FACE",FACE,{"disambiguationData":[OSD([sQuery(id+"F5.wireOp",EDGE,"E51")])]})]});}
            var Q12;
            Q12=makeQuery(id+"F4.boolean.opBoolean","COPY",EDGE,{"derivedFrom":makeQuery(id+"F4.opExtrude","CAP_EDGE",EDGE,{"disambiguationData":[OSD([sQuery(id+"F0.wireOp",EDGE,"E6.MirrorC")])],"isStart":false})});
            var Q13;
            Q13=makeQuery(id+"F4.boolean.opBoolean","COPY",EDGE,{"derivedFrom":makeQuery(id+"F4.opExtrude","CAP_EDGE",EDGE,{"disambiguationData":[OSD([sQuery(id+"F0.wireOp",EDGE,"E7.MirrorC")])],"isStart":false})});
            var Q14;
            Q14=makeQuery(id+"F4.boolean.opBoolean","COPY",EDGE,{"derivedFrom":makeQuery(id+"F4.opExtrude","CAP_EDGE",EDGE,{"disambiguationData":[OSD([sQuery(id+"F0.wireOp",EDGE,"E24")])],"isStart":false})});
            var Q15;
            Q15=makeQuery(id+"F4.boolean.opBoolean","COPY",EDGE,{"derivedFrom":makeQuery(id+"F4.opExtrude","CAP_EDGE",EDGE,{"disambiguationData":[OSD([sQuery(id+"F0.wireOp",EDGE,"E5.MirrorC")])],"isStart":false})});
            fillet(context, id + "F13", {"entities" : qUnion([Q0, Q1, Q2, Q3, Q4, Q5, Q6, Q7, Q8, Q9, Q10, Q11, Q12, Q13, Q14, Q15]), "radius" : 0.64 * mm, "tangentPropagation" : true, "allowEdgeOverflow" : false});
        }
    });
